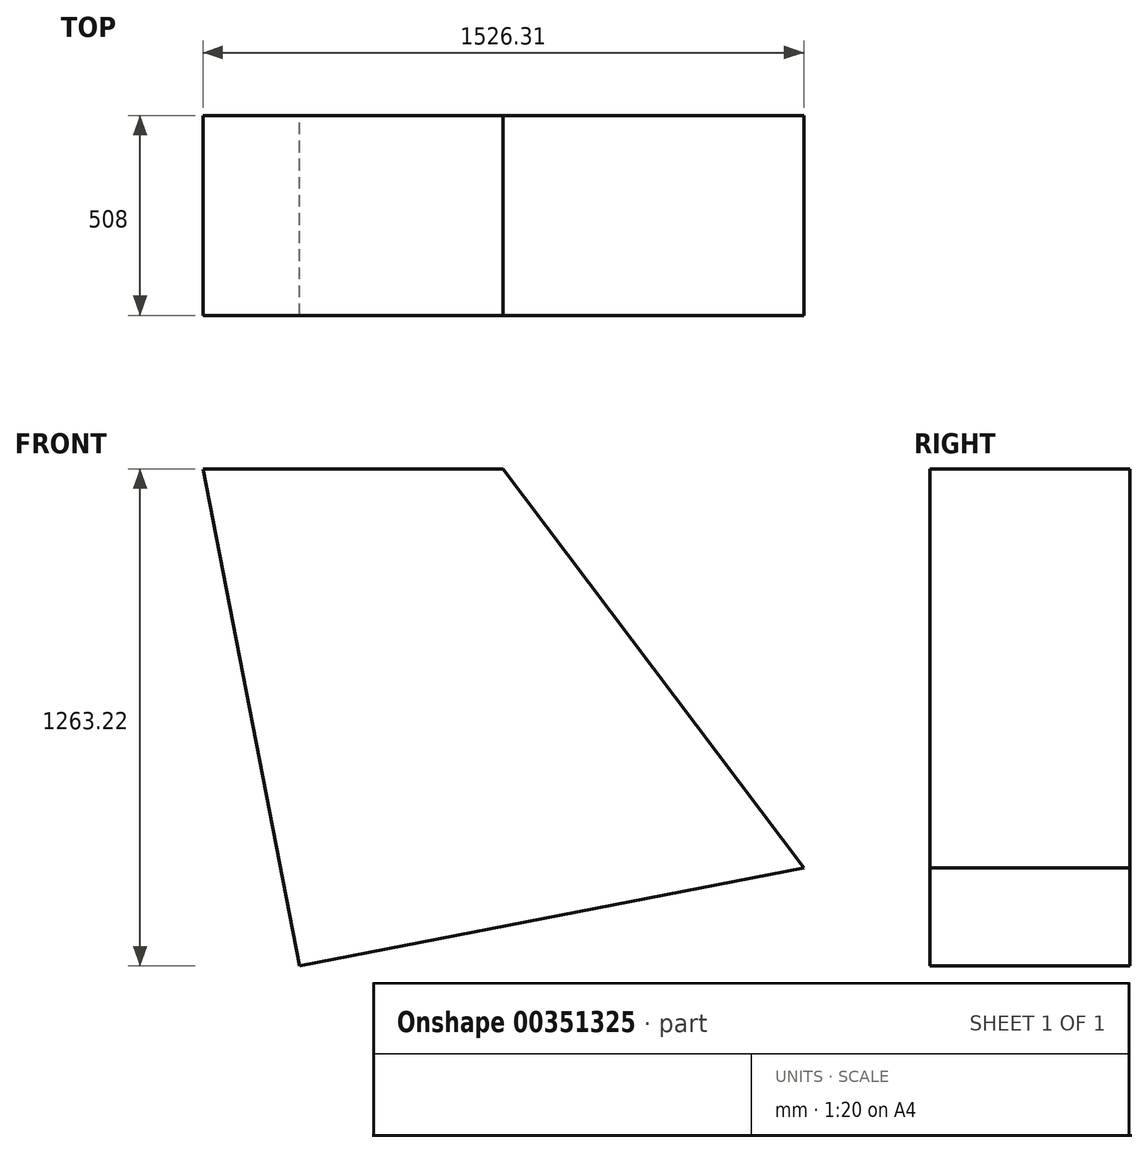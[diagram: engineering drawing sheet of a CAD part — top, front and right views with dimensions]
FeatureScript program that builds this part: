
annotation { "Feature Type Name" : "Feature", "Feature Type Description" : "" }
export const myFeature = defineFeature(function(context is Context, id is Id, definition is map)
    precondition{}
    {
        {
            var Q0;
            Q0=qCreatedBy(makeId("Front.planeOp"),FACE);
            var sketch = newSketch(context, id + "F0", { "sketchPlane" : qUnion([Q0])});
            skLineSegment(sketch, "E0", {"start": v(0, 0) * mm, "end": v(762, 0) * mm});
            skLineSegment(sketch, "E1", {"start": v(762, 0) * mm, "end": v(1526.3, -1014.27) * mm});
            skLineSegment(sketch, "E2", {"start": v(1526.3, -1014.27) * mm, "end": v(245.55, -1263.22) * mm});
            skLineSegment(sketch, "E3", {"start": v(245.55, -1263.22) * mm, "end": v(0, 0) * mm});
            skSolve(sketch);
        }
        {
            var Q0;
            Q0 = qSketchRegion(id + "F0", true);
            extrude(context, id + "F1", {"entities" : qUnion([Q0]), "depth" : 508 * mm});
        }
    });
